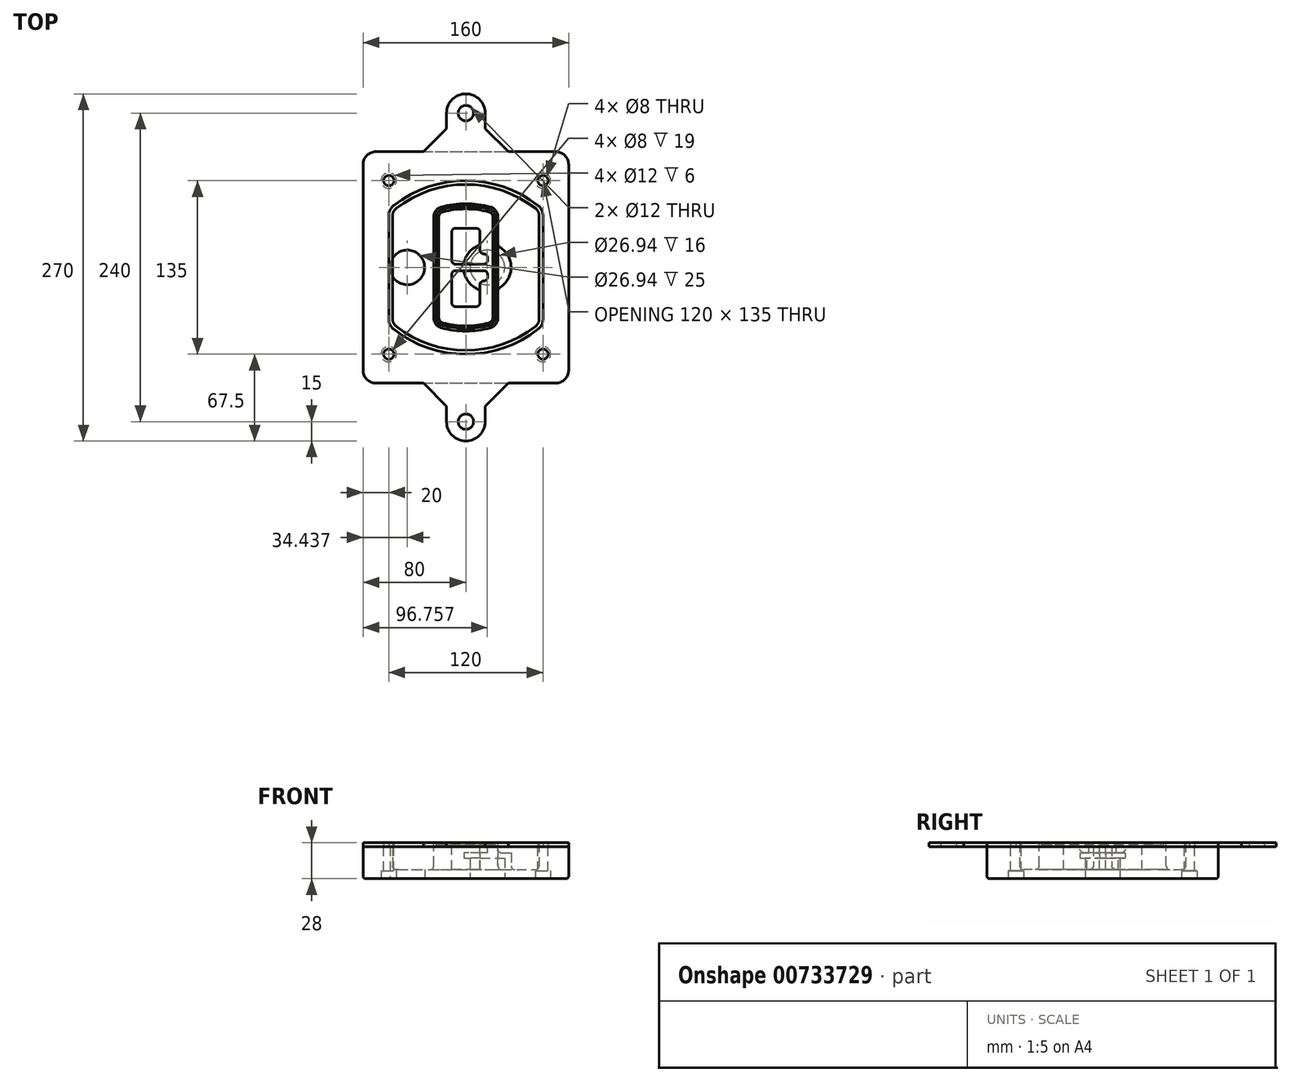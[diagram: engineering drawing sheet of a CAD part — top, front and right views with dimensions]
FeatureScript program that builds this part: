
annotation { "Feature Type Name" : "Feature", "Feature Type Description" : "" }
export const myFeature = defineFeature(function(context is Context, id is Id, definition is map)
    precondition{}
    {
        {
            var Q0;
            Q0=qCreatedBy(makeId("Top.planeOp"),FACE);
            var sketch = newSketch(context, id + "F0", { "sketchPlane" : qUnion([Q0])});
            skPoint(sketch, "E0.rect.middle", {"position": v(0, 0) * mm});
            skLineSegment(sketch, "E1.bottom", {"start": v(-70, -90) * mm, "end": v(70, -90) * mm});
            skLineSegment(sketch, "E1.top", {"start": v(-70, 90) * mm, "end": v(70, 90) * mm});
            skLineSegment(sketch, "E1.left", {"start": v(-80, -80) * mm, "end": v(-80, 80) * mm});
            skLineSegment(sketch, "E1.right", {"start": v(80, -80) * mm, "end": v(80, 80) * mm});
            skLineSegment(sketch, "E2", {"start": v(-80, 90) * mm, "end": v(80, -90) * mm, "construction": true});
            skLineSegment(sketch, "E3", {"start": v(80, 90) * mm, "end": v(-80, -90) * mm, "construction": true});
            skCircle(sketch, "E4", {"center": v(-60, 67.5) * mm, "radius": 4 * mm});
            skCircle(sketch, "E5", {"center": v(60, 67.5) * mm, "radius": 4 * mm});
            skCircle(sketch, "E6", {"center": v(60, -67.5) * mm, "radius": 4 * mm});
            skCircle(sketch, "E7", {"center": v(-60, -67.5) * mm, "radius": 4 * mm});
            skLineSegment(sketch, "E8", {"start": v(-60, 67.5) * mm, "end": v(60, 67.5) * mm, "construction": true});
            skLineSegment(sketch, "E9", {"start": v(60, 67.5) * mm, "end": v(60, -67.5) * mm, "construction": true});
            skLineSegment(sketch, "E10", {"start": v(60, -67.5) * mm, "end": v(-60, -67.5) * mm, "construction": true});
            skLineSegment(sketch, "E11", {"start": v(-60, -67.5) * mm, "end": v(-60, 67.5) * mm, "construction": true});
            skLineSegment(sketch, "E12", {"start": v(-60, 40.3) * mm, "end": v(-60, -40.3) * mm});
            skLineSegment(sketch, "E13", {"start": v(60, 40.3) * mm, "end": v(60, -40.3) * mm});
            skArc(sketch, "E14", {"start": v(56.15, 48.18) * mm, "mid": v(0, 67.5) * mm, "end": v(-56.15, 48.18) * mm});
            skArc(sketch, "E15", {"start": v(-56.15, -48.18) * mm, "mid": v(0, -67.5) * mm, "end": v(56.15, -48.18) * mm});
            skLineSegment(sketch, "E16", {"start": v(-60, 0) * mm, "end": v(60, 0) * mm, "construction": true});
            skPoint(sketch, "E17.visualSharp", {"position": v(-60, -45) * mm});
            skArc(sketch, "E17.filletArc", {"start": v(-60, -40.3) * mm, "mid": v(-58.99, -44.68) * mm, "end": v(-56.15, -48.18) * mm});
            skPoint(sketch, "E18.visualSharp", {"position": v(-60, 45) * mm});
            skArc(sketch, "E18.filletArc", {"start": v(-56.15, 48.18) * mm, "mid": v(-58.99, 44.68) * mm, "end": v(-60, 40.3) * mm});
            skPoint(sketch, "E19.visualSharp", {"position": v(60, 45) * mm});
            skArc(sketch, "E19.filletArc", {"start": v(60, 40.3) * mm, "mid": v(58.99, 44.68) * mm, "end": v(56.15, 48.18) * mm});
            skPoint(sketch, "E20.visualSharp", {"position": v(60, -45) * mm});
            skArc(sketch, "E20.filletArc", {"start": v(56.15, -48.18) * mm, "mid": v(58.99, -44.68) * mm, "end": v(60, -40.3) * mm});
            skPoint(sketch, "E21.visualSharp", {"position": v(-80, 90) * mm});
            skArc(sketch, "E21.filletArc", {"start": v(-70, 90) * mm, "mid": v(-77.07, 87.07) * mm, "end": v(-80, 80) * mm});
            skPoint(sketch, "E22.visualSharp", {"position": v(80, 90) * mm});
            skArc(sketch, "E22.filletArc", {"start": v(80, 80) * mm, "mid": v(77.07, 87.07) * mm, "end": v(70, 90) * mm});
            skPoint(sketch, "E23.visualSharp", {"position": v(80, -90) * mm});
            skArc(sketch, "E23.filletArc", {"start": v(70, -90) * mm, "mid": v(77.07, -87.07) * mm, "end": v(80, -80) * mm});
            skPoint(sketch, "E24.visualSharp", {"position": v(-80, -90) * mm});
            skArc(sketch, "E24.filletArc", {"start": v(-80, -80) * mm, "mid": v(-77.07, -87.07) * mm, "end": v(-70, -90) * mm});
            skArc(sketch, "E25.0", {"start": v(57, 40.3) * mm, "mid": v(56.3, 43.36) * mm, "end": v(54.3, 45.81) * mm});
            skLineSegment(sketch, "E25.1", {"start": v(57, 40.3) * mm, "end": v(57, -40.3) * mm});
            skArc(sketch, "E25.2", {"start": v(54.3, -45.81) * mm, "mid": v(56.3, -43.36) * mm, "end": v(57, -40.3) * mm});
            skArc(sketch, "E25.3", {"start": v(-54.3, -45.81) * mm, "mid": v(0, -64.5) * mm, "end": v(54.3, -45.81) * mm});
            skArc(sketch, "E25.4", {"start": v(-57, -40.3) * mm, "mid": v(-56.3, -43.36) * mm, "end": v(-54.3, -45.81) * mm});
            skArc(sketch, "E25.5", {"start": v(54.3, 45.81) * mm, "mid": v(0, 64.5) * mm, "end": v(-54.3, 45.81) * mm});
            skLineSegment(sketch, "E25.6", {"start": v(-57, 40.3) * mm, "end": v(-57, -40.3) * mm});
            skArc(sketch, "E25.7", {"start": v(-54.3, 45.81) * mm, "mid": v(-56.3, 43.36) * mm, "end": v(-57, 40.3) * mm});
            skArc(sketch, "E26.0", {"start": v(-58.62, 51.33) * mm, "mid": v(-62.58, 46.43) * mm, "end": v(-64, 40.3) * mm});
            skArc(sketch, "E26.1", {"start": v(58.62, 51.33) * mm, "mid": v(0, 71.5) * mm, "end": v(-58.62, 51.33) * mm});
            skArc(sketch, "E26.2", {"start": v(64, 40.3) * mm, "mid": v(62.58, 46.43) * mm, "end": v(58.62, 51.33) * mm});
            skLineSegment(sketch, "E26.3", {"start": v(64, 40.3) * mm, "end": v(64, -40.3) * mm});
            skArc(sketch, "E26.4", {"start": v(58.62, -51.33) * mm, "mid": v(62.58, -46.43) * mm, "end": v(64, -40.3) * mm});
            skLineSegment(sketch, "E26.5", {"start": v(-64, 40.3) * mm, "end": v(-64, -40.3) * mm});
            skArc(sketch, "E26.6", {"start": v(-58.62, -51.33) * mm, "mid": v(0, -71.5) * mm, "end": v(58.62, -51.33) * mm});
            skArc(sketch, "E26.7", {"start": v(-64, -40.3) * mm, "mid": v(-62.58, -46.43) * mm, "end": v(-58.62, -51.33) * mm});
            skSolve(sketch);
        }
        {
            var Q0;
            Q0=makeQuery(id+"F0.imprint","IMPRINT",FACE,{"disambiguationData":[TD([[makeQuery(id+"F0.imprint","IMPRINT",EDGE,{"derivedFrom":sQuery(id+"F0.wireOp",EDGE,"E1.bottom")}),1.0]])]});
            var Q1;
            Q1=makeQuery(id+"F0.imprint","IMPRINT",FACE,{"disambiguationData":[TD([[makeQuery(id+"F0.imprint","IMPRINT",EDGE,{"derivedFrom":sQuery(id+"F0.wireOp",EDGE,"E12")}),1.0]])]});
            var Q2;
            Q2=makeQuery(id+"F0.imprint","IMPRINT",FACE,{"disambiguationData":[TD([[makeQuery(id+"F0.imprint","IMPRINT",EDGE,{"derivedFrom":sQuery(id+"F0.wireOp",EDGE,"E25.0")}),1.0]])]});
            var Q3;
            Q3=makeQuery(id+"F0.imprint","IMPRINT",FACE,{"disambiguationData":[TD([[makeQuery(id+"F0.imprint","IMPRINT",EDGE,{"derivedFrom":sQuery(id+"F0.wireOp",EDGE,"E12")}),-1.0]])]});
            extrude(context, id + "F1", {"entities" : qUnion([Q0, Q1, Q2, Q3]), "oppositeDirection" : true, "depth" : 25 * mm});
        }
        {
            var Q0;
            Q0=makeQuery(id+"F0.imprint","IMPRINT",FACE,{"disambiguationData":[TD([[makeQuery(id+"F0.imprint","IMPRINT",EDGE,{"derivedFrom":sQuery(id+"F0.wireOp",EDGE,"E12")}),1.0]])]});
            extrude(context, id + "F2", {"entities" : qUnion([Q0]), "operationType" : NewBodyOperationType.ADD, "depth" : 3 * mm});
        }
        {
            var Q0;
            Q0=makeQuery(id+"F0.imprint","IMPRINT",FACE,{"disambiguationData":[TD([[makeQuery(id+"F0.imprint","IMPRINT",EDGE,{"derivedFrom":sQuery(id+"F0.wireOp",EDGE,"E25.0")}),1.0]])]});
            extrude(context, id + "F3", {"entities" : qUnion([Q0]), "operationType" : NewBodyOperationType.REMOVE, "oppositeDirection" : true, "depth" : 18 * mm});
        }
        {
            var Q0;
            Q0=makeQuery(id+"F2.opExtrude","CAP_FACE",FACE,{"disambiguationData":[OSD([sQuery(id+"F0.wireOp",EDGE,"E12"),sQuery(id+"F0.wireOp",EDGE,"E13"),sQuery(id+"F0.wireOp",EDGE,"E14"),sQuery(id+"F0.wireOp",EDGE,"E15"),sQuery(id+"F0.wireOp",EDGE,"E17.filletArc"),sQuery(id+"F0.wireOp",EDGE,"E18.filletArc"),sQuery(id+"F0.wireOp",EDGE,"E19.filletArc"),sQuery(id+"F0.wireOp",EDGE,"E20.filletArc"),sQuery(id+"F0.wireOp",EDGE,"E25.0"),sQuery(id+"F0.wireOp",EDGE,"E25.1"),sQuery(id+"F0.wireOp",EDGE,"E25.2"),sQuery(id+"F0.wireOp",EDGE,"E25.3"),sQuery(id+"F0.wireOp",EDGE,"E25.4"),sQuery(id+"F0.wireOp",EDGE,"E25.5"),sQuery(id+"F0.wireOp",EDGE,"E25.6"),sQuery(id+"F0.wireOp",EDGE,"E25.7")])],"isStart":false});
            var sketch = newSketch(context, id + "F4", { "sketchPlane" : qUnion([Q0])});
            skArc(sketch, "E27.0", {"start": v(-19.08, -46.97) * mm, "mid": v(0, -49.5) * mm, "end": v(19.08, -46.97) * mm});
            skArc(sketch, "E28.0", {"start": v(19.08, 46.97) * mm, "mid": v(0, 49.5) * mm, "end": v(-19.08, 46.97) * mm});
            skLineSegment(sketch, "E29", {"start": v(-25, 39.25) * mm, "end": v(-25, -39.25) * mm});
            skLineSegment(sketch, "E30", {"start": v(25, 39.25) * mm, "end": v(25, -39.25) * mm});
            skLineSegment(sketch, "E31", {"start": v(-25, 45.1) * mm, "end": v(25, 45.1) * mm, "construction": true});
            skLineSegment(sketch, "E32", {"start": v(-25, -45.1) * mm, "end": v(25, -45.1) * mm, "construction": true});
            skPoint(sketch, "E33.visualSharp", {"position": v(-25, 45.1) * mm});
            skArc(sketch, "E33.filletArc", {"start": v(-19.08, 46.97) * mm, "mid": v(-23.35, 44.11) * mm, "end": v(-25, 39.25) * mm});
            skPoint(sketch, "E34.visualSharp", {"position": v(25, 45.1) * mm});
            skArc(sketch, "E34.filletArc", {"start": v(25, 39.25) * mm, "mid": v(23.35, 44.11) * mm, "end": v(19.08, 46.97) * mm});
            skPoint(sketch, "E35.visualSharp", {"position": v(25, -45.1) * mm});
            skArc(sketch, "E35.filletArc", {"start": v(19.08, -46.97) * mm, "mid": v(23.35, -44.11) * mm, "end": v(25, -39.25) * mm});
            skPoint(sketch, "E36.visualSharp", {"position": v(-25, -45.1) * mm});
            skArc(sketch, "E36.filletArc", {"start": v(-25, -39.25) * mm, "mid": v(-23.35, -44.11) * mm, "end": v(-19.08, -46.97) * mm});
            skArc(sketch, "E37.0", {"start": v(54.3, 45.81) * mm, "mid": v(0, 64.5) * mm, "end": v(-54.3, 45.81) * mm});
            skArc(sketch, "E37.1", {"start": v(-54.3, 45.81) * mm, "mid": v(-56.3, 43.36) * mm, "end": v(-57, 40.3) * mm});
            skLineSegment(sketch, "E37.2", {"start": v(-57, 40.3) * mm, "end": v(-57, -40.3) * mm});
            skArc(sketch, "E37.3", {"start": v(-57, -40.3) * mm, "mid": v(-56.3, -43.36) * mm, "end": v(-54.3, -45.81) * mm});
            skArc(sketch, "E37.4", {"start": v(-54.3, -45.81) * mm, "mid": v(0, -64.5) * mm, "end": v(54.3, -45.81) * mm});
            skArc(sketch, "E37.5", {"start": v(54.3, -45.81) * mm, "mid": v(56.3, -43.36) * mm, "end": v(57, -40.3) * mm});
            skLineSegment(sketch, "E37.6", {"start": v(57, 40.3) * mm, "end": v(57, -40.3) * mm});
            skArc(sketch, "E37.7", {"start": v(57, 40.3) * mm, "mid": v(56.3, 43.36) * mm, "end": v(54.3, 45.81) * mm});
            skLineSegment(sketch, "E38.0", {"start": v(23, 39.25) * mm, "end": v(23, -39.25) * mm});
            skArc(sketch, "E38.1", {"start": v(18.56, -45.04) * mm, "mid": v(21.76, -42.9) * mm, "end": v(23, -39.25) * mm});
            skArc(sketch, "E38.2", {"start": v(-18.56, -45.04) * mm, "mid": v(0, -47.5) * mm, "end": v(18.56, -45.04) * mm});
            skArc(sketch, "E38.3", {"start": v(-23, -39.25) * mm, "mid": v(-21.76, -42.9) * mm, "end": v(-18.56, -45.04) * mm});
            skLineSegment(sketch, "E38.4", {"start": v(-23, 39.25) * mm, "end": v(-23, -39.25) * mm});
            skArc(sketch, "E38.5", {"start": v(23, 39.25) * mm, "mid": v(21.76, 42.9) * mm, "end": v(18.56, 45.04) * mm});
            skArc(sketch, "E38.6", {"start": v(-18.56, 45.04) * mm, "mid": v(-21.76, 42.9) * mm, "end": v(-23, 39.25) * mm});
            skArc(sketch, "E38.7", {"start": v(18.56, 45.04) * mm, "mid": v(0, 47.5) * mm, "end": v(-18.56, 45.04) * mm});
            skArc(sketch, "E39.0", {"start": v(21, 39.25) * mm, "mid": v(20.18, 41.68) * mm, "end": v(18.04, 43.1) * mm});
            skLineSegment(sketch, "E39.1", {"start": v(21, 39.25) * mm, "end": v(21, -39.25) * mm});
            skArc(sketch, "E39.2", {"start": v(18.04, -43.1) * mm, "mid": v(20.18, -41.68) * mm, "end": v(21, -39.25) * mm});
            skArc(sketch, "E39.3", {"start": v(-18.04, -43.1) * mm, "mid": v(0, -45.5) * mm, "end": v(18.04, -43.1) * mm});
            skArc(sketch, "E39.4", {"start": v(-21, -39.25) * mm, "mid": v(-20.18, -41.68) * mm, "end": v(-18.04, -43.1) * mm});
            skArc(sketch, "E39.5", {"start": v(18.04, 43.1) * mm, "mid": v(0, 45.5) * mm, "end": v(-18.04, 43.1) * mm});
            skLineSegment(sketch, "E39.6", {"start": v(-21, 39.25) * mm, "end": v(-21, -39.25) * mm});
            skArc(sketch, "E39.7", {"start": v(-18.04, 43.1) * mm, "mid": v(-20.18, 41.68) * mm, "end": v(-21, 39.25) * mm});
            skLineSegment(sketch, "E40", {"start": v(-25, 0) * mm, "end": v(25, 0) * mm, "construction": true});
            skLineSegment(sketch, "E41", {"start": v(-11, 5.5) * mm, "end": v(-11, 27.5) * mm});
            skLineSegment(sketch, "E42", {"start": v(-8, 30.5) * mm, "end": v(8, 30.5) * mm});
            skLineSegment(sketch, "E43", {"start": v(11, 27.5) * mm, "end": v(11, 13.5) * mm});
            skLineSegment(sketch, "E44", {"start": v(14, 10.5) * mm, "end": v(14, 10.5) * mm});
            skLineSegment(sketch, "E45", {"start": v(17, 7.5) * mm, "end": v(17, 5.5) * mm});
            skLineSegment(sketch, "E46", {"start": v(14, 2.5) * mm, "end": v(-8, 2.5) * mm});
            skPoint(sketch, "E47.visualSharp", {"position": v(-11, 30.5) * mm});
            skArc(sketch, "E47.filletArc", {"start": v(-8, 30.5) * mm, "mid": v(-10.12, 29.62) * mm, "end": v(-11, 27.5) * mm});
            skPoint(sketch, "E48.visualSharp", {"position": v(11, 30.5) * mm});
            skArc(sketch, "E48.filletArc", {"start": v(11, 27.5) * mm, "mid": v(10.12, 29.62) * mm, "end": v(8, 30.5) * mm});
            skPoint(sketch, "E49.visualSharp", {"position": v(11, 10.5) * mm});
            skArc(sketch, "E49.filletArc", {"start": v(11, 13.5) * mm, "mid": v(11.88, 11.38) * mm, "end": v(14, 10.5) * mm});
            skPoint(sketch, "E50.visualSharp", {"position": v(17, 10.5) * mm});
            skArc(sketch, "E50.filletArc", {"start": v(17, 7.5) * mm, "mid": v(16.12, 9.62) * mm, "end": v(14, 10.5) * mm});
            skPoint(sketch, "E51.visualSharp", {"position": v(17, 2.5) * mm});
            skArc(sketch, "E51.filletArc", {"start": v(14, 2.5) * mm, "mid": v(16.12, 3.38) * mm, "end": v(17, 5.5) * mm});
            skPoint(sketch, "E52.visualSharp", {"position": v(-11, 2.5) * mm});
            skArc(sketch, "E52.filletArc", {"start": v(-11, 5.5) * mm, "mid": v(-10.12, 3.38) * mm, "end": v(-8, 2.5) * mm});
            skLineSegment(sketch, "E53.0.MirrorCS", {"start": v(14, -2.5) * mm, "end": v(-8, -2.5) * mm});
            skArc(sketch, "E54.0.MirrorCS", {"start": v(-11, -5.5) * mm, "mid": v(-10.12, -3.38) * mm, "end": v(-8, -2.5) * mm});
            skLineSegment(sketch, "E55.0.MirrorCS", {"start": v(-11, -5.5) * mm, "end": v(-11, -27.5) * mm});
            skArc(sketch, "E56.0.MirrorCS", {"start": v(-8, -30.5) * mm, "mid": v(-10.12, -29.62) * mm, "end": v(-11, -27.5) * mm});
            skLineSegment(sketch, "E57.0.MirrorCS", {"start": v(-8, -30.5) * mm, "end": v(8, -30.5) * mm});
            skArc(sketch, "E58.0.MirrorCS", {"start": v(11, -27.5) * mm, "mid": v(10.12, -29.62) * mm, "end": v(8, -30.5) * mm});
            skLineSegment(sketch, "E59.0.MirrorCS", {"start": v(11, -27.5) * mm, "end": v(11, -13.5) * mm});
            skArc(sketch, "E60.0.MirrorCS", {"start": v(11, -13.5) * mm, "mid": v(11.88, -11.38) * mm, "end": v(14, -10.5) * mm});
            skArc(sketch, "E61.0.MirrorCS", {"start": v(17, -7.5) * mm, "mid": v(16.12, -9.62) * mm, "end": v(14, -10.5) * mm});
            skLineSegment(sketch, "E62.0.MirrorCS", {"start": v(17, -7.5) * mm, "end": v(17, -5.5) * mm});
            skArc(sketch, "E63.0.MirrorCS", {"start": v(14, -2.5) * mm, "mid": v(16.12, -3.38) * mm, "end": v(17, -5.5) * mm});
            skSolve(sketch);
        }
        {
            var Q0;
            Q0=makeQuery(id+"F4.imprint","IMPRINT",FACE,{"disambiguationData":[TD([[makeQuery(id+"F4.imprint","IMPRINT",EDGE,{"derivedFrom":sQuery(id+"F4.wireOp",EDGE,"E27.0")}),1.0]])]});
            var Q1;
            Q1=makeQuery(id+"F4.imprint","IMPRINT",FACE,{"disambiguationData":[TD([[makeQuery(id+"F4.imprint","IMPRINT",EDGE,{"derivedFrom":sQuery(id+"F4.wireOp",EDGE,"E38.0")}),-1.0]])]});
            var Q2;
            Q2=makeQuery(id+"F4.imprint","IMPRINT",FACE,{"disambiguationData":[TD([[makeQuery(id+"F4.imprint","IMPRINT",EDGE,{"derivedFrom":sQuery(id+"F4.wireOp",EDGE,"E39.0")}),1.0]])]});
            extrude(context, id + "F5", {"entities" : qUnion([Q0, Q1, Q2]), "operationType" : NewBodyOperationType.ADD, "endBound" : BoundingType.UP_TO_NEXT, "oppositeDirection" : true, "depth" : 25 * mm});
        }
        {
            var Q0;
            Q0=makeQuery(id+"F4.imprint","IMPRINT",FACE,{"disambiguationData":[TD([[makeQuery(id+"F4.imprint","IMPRINT",EDGE,{"derivedFrom":sQuery(id+"F4.wireOp",EDGE,"E38.0")}),-1.0]])]});
            extrude(context, id + "F6", {"entities" : qUnion([Q0]), "operationType" : NewBodyOperationType.REMOVE, "oppositeDirection" : true, "depth" : 2 * mm});
        }
        {
            var Q0;
            Q0=makeQuery(id+"F1.opExtrude","CAP_FACE",FACE,{"disambiguationData":[OSD([sQuery(id+"F0.wireOp",EDGE,"E1.bottom"),sQuery(id+"F0.wireOp",EDGE,"E1.top"),sQuery(id+"F0.wireOp",EDGE,"E1.left"),sQuery(id+"F0.wireOp",EDGE,"E1.right"),sQuery(id+"F0.wireOp",EDGE,"E4"),sQuery(id+"F0.wireOp",EDGE,"E5"),sQuery(id+"F0.wireOp",EDGE,"E6"),sQuery(id+"F0.wireOp",EDGE,"E7"),sQuery(id+"F0.wireOp",EDGE,"E21.filletArc"),sQuery(id+"F0.wireOp",EDGE,"E22.filletArc"),sQuery(id+"F0.wireOp",EDGE,"E23.filletArc"),sQuery(id+"F0.wireOp",EDGE,"E24.filletArc")])],"isStart":false});
            var sketch = newSketch(context, id + "F7", { "sketchPlane" : qUnion([Q0])});
            skCircle(sketch, "E64", {"center": v(16.76, 0) * mm, "radius": 13.47 * mm});
            skCircle(sketch, "E65", {"center": v(-45.56, 0) * mm, "radius": 13.47 * mm});
            skLineSegment(sketch, "E66", {"start": v(80, 0) * mm, "end": v(-80, 0) * mm});
            skCircle(sketch, "E67", {"center": v(16.76, 0) * mm, "radius": 18.47 * mm});
            skCircle(sketch, "E68", {"center": v(60, -67.5) * mm, "radius": 6 * mm});
            skCircle(sketch, "E69", {"center": v(-60, -67.5) * mm, "radius": 6 * mm});
            skCircle(sketch, "E70", {"center": v(-60, 67.5) * mm, "radius": 6 * mm});
            skCircle(sketch, "E71", {"center": v(60, 67.5) * mm, "radius": 6 * mm});
            skSolve(sketch);
        }
        {
            var Q0;
            {var subQ1=sQuery(id+"F7.wireOp",EDGE,"E66");var subQ4=sQuery(id+"F7.wireOp",EDGE,"E64");var subQ6=makeQuery(id+"F7.imprint","INTERSECT",VERTEX,{"disambiguationData":[OD(0.0)],"derivedFrom":[subQ4,subQ1]});Q0=makeQuery(id+"F7.imprint","IMPRINT",FACE,{"disambiguationData":[TD([[makeQuery(id+"F7.imprint","IMPRINT",EDGE,{"disambiguationData":[TD([[subQ6,-1.0]])],"derivedFrom":subQ4}),-1.0]])]});}
            var Q1;
            {var subQ0=sQuery(id+"F7.wireOp",EDGE,"E66");var subQ1=sQuery(id+"F7.wireOp",EDGE,"E64");var subQ3=makeQuery(id+"F7.imprint","INTERSECT",VERTEX,{"disambiguationData":[OD(0.0)],"derivedFrom":[subQ1,subQ0]});Q1=makeQuery(id+"F7.imprint","IMPRINT",FACE,{"disambiguationData":[TD([[makeQuery(id+"F7.imprint","IMPRINT",EDGE,{"disambiguationData":[TD([[subQ3,-1.0]])],"derivedFrom":subQ1}),1.0]])]});}
            var Q2;
            {var subQ0=sQuery(id+"F7.wireOp",EDGE,"E66");var subQ1=sQuery(id+"F7.wireOp",EDGE,"E64");var subQ3=makeQuery(id+"F7.imprint","INTERSECT",VERTEX,{"disambiguationData":[OD(0.0)],"derivedFrom":[subQ1,subQ0]});Q2=makeQuery(id+"F7.imprint","IMPRINT",FACE,{"disambiguationData":[TD([[makeQuery(id+"F7.imprint","IMPRINT",EDGE,{"disambiguationData":[TD([[subQ3,1.0]])],"derivedFrom":subQ1}),1.0]])]});}
            var Q3;
            {var subQ1=sQuery(id+"F7.wireOp",EDGE,"E66");var subQ4=sQuery(id+"F7.wireOp",EDGE,"E64");var subQ6=makeQuery(id+"F7.imprint","INTERSECT",VERTEX,{"disambiguationData":[OD(0.0)],"derivedFrom":[subQ4,subQ1]});Q3=makeQuery(id+"F7.imprint","IMPRINT",FACE,{"disambiguationData":[TD([[makeQuery(id+"F7.imprint","IMPRINT",EDGE,{"disambiguationData":[TD([[subQ6,1.0]])],"derivedFrom":subQ4}),-1.0]])]});}
            extrude(context, id + "F8", {"entities" : qUnion([Q0, Q1, Q2, Q3]), "operationType" : NewBodyOperationType.ADD, "oppositeDirection" : true, "depth" : 20 * mm});
        }
        {
            var Q0;
            {var subQ0=sQuery(id+"F7.wireOp",EDGE,"E66");var subQ1=sQuery(id+"F7.wireOp",EDGE,"E64");var subQ3=makeQuery(id+"F7.imprint","INTERSECT",VERTEX,{"disambiguationData":[OD(0.0)],"derivedFrom":[subQ1,subQ0]});Q0=makeQuery(id+"F7.imprint","IMPRINT",FACE,{"disambiguationData":[TD([[makeQuery(id+"F7.imprint","IMPRINT",EDGE,{"disambiguationData":[TD([[subQ3,-1.0]])],"derivedFrom":subQ1}),1.0]])]});}
            var Q1;
            {var subQ0=sQuery(id+"F7.wireOp",EDGE,"E66");var subQ1=sQuery(id+"F7.wireOp",EDGE,"E64");var subQ3=makeQuery(id+"F7.imprint","INTERSECT",VERTEX,{"disambiguationData":[OD(0.0)],"derivedFrom":[subQ1,subQ0]});Q1=makeQuery(id+"F7.imprint","IMPRINT",FACE,{"disambiguationData":[TD([[makeQuery(id+"F7.imprint","IMPRINT",EDGE,{"disambiguationData":[TD([[subQ3,1.0]])],"derivedFrom":subQ1}),1.0]])]});}
            extrude(context, id + "F9", {"entities" : qUnion([Q0, Q1]), "operationType" : NewBodyOperationType.REMOVE, "oppositeDirection" : true, "depth" : 16 * mm});
        }
        {
            var Q0;
            {var subQ0=sQuery(id+"F7.wireOp",EDGE,"E66");var subQ1=sQuery(id+"F7.wireOp",EDGE,"E65");var subQ3=makeQuery(id+"F7.imprint","INTERSECT",VERTEX,{"disambiguationData":[OD(0.0)],"derivedFrom":[subQ1,subQ0]});Q0=makeQuery(id+"F7.imprint","IMPRINT",FACE,{"disambiguationData":[TD([[makeQuery(id+"F7.imprint","IMPRINT",EDGE,{"disambiguationData":[TD([[subQ3,-1.0]])],"derivedFrom":subQ1}),1.0]])]});}
            var Q1;
            {var subQ0=sQuery(id+"F7.wireOp",EDGE,"E66");var subQ1=sQuery(id+"F7.wireOp",EDGE,"E65");var subQ3=makeQuery(id+"F7.imprint","INTERSECT",VERTEX,{"disambiguationData":[OD(0.0)],"derivedFrom":[subQ1,subQ0]});Q1=makeQuery(id+"F7.imprint","IMPRINT",FACE,{"disambiguationData":[TD([[makeQuery(id+"F7.imprint","IMPRINT",EDGE,{"disambiguationData":[TD([[subQ3,1.0]])],"derivedFrom":subQ1}),1.0]])]});}
            extrude(context, id + "F10", {"entities" : qUnion([Q0, Q1]), "operationType" : NewBodyOperationType.REMOVE, "oppositeDirection" : true, "depth" : 25 * mm});
        }
        {
            var Q0;
            Q0=makeQuery(id+"F7.imprint","IMPRINT",FACE,{"disambiguationData":[TD([[makeQuery(id+"F7.imprint","IMPRINT",EDGE,{"derivedFrom":sQuery(id+"F7.wireOp",EDGE,"E68")}),1.0]])]});
            var Q1;
            Q1=makeQuery(id+"F7.imprint","IMPRINT",FACE,{"disambiguationData":[TD([[makeQuery(id+"F7.imprint","IMPRINT",EDGE,{"derivedFrom":makeQuery(id+"F1.opExtrude","CAP_EDGE",EDGE,{"disambiguationData":[OSD([sQuery(id+"F0.wireOp",EDGE,"E5")])],"isStart":false})}),-1.0]])]});
            var Q2;
            Q2=makeQuery(id+"F7.imprint","IMPRINT",FACE,{"disambiguationData":[TD([[makeQuery(id+"F7.imprint","IMPRINT",EDGE,{"derivedFrom":sQuery(id+"F7.wireOp",EDGE,"E69")}),1.0]])]});
            var Q3;
            Q3=makeQuery(id+"F7.imprint","IMPRINT",FACE,{"disambiguationData":[TD([[makeQuery(id+"F7.imprint","IMPRINT",EDGE,{"derivedFrom":makeQuery(id+"F1.opExtrude","CAP_EDGE",EDGE,{"disambiguationData":[OSD([sQuery(id+"F0.wireOp",EDGE,"E4")])],"isStart":false})}),-1.0]])]});
            var Q4;
            Q4=makeQuery(id+"F7.imprint","IMPRINT",FACE,{"disambiguationData":[TD([[makeQuery(id+"F7.imprint","IMPRINT",EDGE,{"derivedFrom":sQuery(id+"F7.wireOp",EDGE,"E70")}),1.0]])]});
            var Q5;
            Q5=makeQuery(id+"F7.imprint","IMPRINT",FACE,{"disambiguationData":[TD([[makeQuery(id+"F7.imprint","IMPRINT",EDGE,{"derivedFrom":makeQuery(id+"F1.opExtrude","CAP_EDGE",EDGE,{"disambiguationData":[OSD([sQuery(id+"F0.wireOp",EDGE,"E7")])],"isStart":false})}),-1.0]])]});
            var Q6;
            Q6=makeQuery(id+"F7.imprint","IMPRINT",FACE,{"disambiguationData":[TD([[makeQuery(id+"F7.imprint","IMPRINT",EDGE,{"derivedFrom":sQuery(id+"F7.wireOp",EDGE,"E71")}),1.0]])]});
            var Q7;
            Q7=makeQuery(id+"F7.imprint","IMPRINT",FACE,{"disambiguationData":[TD([[makeQuery(id+"F7.imprint","IMPRINT",EDGE,{"derivedFrom":makeQuery(id+"F1.opExtrude","CAP_EDGE",EDGE,{"disambiguationData":[OSD([sQuery(id+"F0.wireOp",EDGE,"E6")])],"isStart":false})}),-1.0]])]});
            extrude(context, id + "F11", {"entities" : qUnion([Q0, Q1, Q2, Q3, Q4, Q5, Q6, Q7]), "operationType" : NewBodyOperationType.REMOVE, "oppositeDirection" : true, "depth" : 6 * mm});
        }
        {
            var Q0;
            Q0=makeQuery(id+"F9.boolean.opBoolean","COPY",FACE,{"derivedFrom":makeQuery(id+"F9.opExtrude","CAP_FACE",FACE,{"disambiguationData":[OSD([sQuery(id+"F7.wireOp",EDGE,"E64")])],"isStart":false})});
            var sketch = newSketch(context, id + "F12", { "sketchPlane" : qUnion([Q0])});
            skArc(sketch, "E72.0", {"start": v(11, 17.55) * mm, "mid": v(2.57, 11.82) * mm, "end": v(-1.54, 2.5) * mm});
            skArc(sketch, "E72.1", {"start": v(-1.54, -2.5) * mm, "mid": v(2.57, -11.82) * mm, "end": v(11, -17.55) * mm});
            skLineSegment(sketch, "E73", {"start": v(-1.54, -2.5) * mm, "end": v(14, -2.5) * mm});
            skLineSegment(sketch, "E74.0", {"start": v(14, 2.5) * mm, "end": v(-1.54, 2.5) * mm});
            skArc(sketch, "E74.1", {"start": v(14, 2.5) * mm, "mid": v(16.12, 3.38) * mm, "end": v(17, 5.5) * mm});
            skLineSegment(sketch, "E74.2", {"start": v(17, 7.5) * mm, "end": v(17, 5.5) * mm});
            skArc(sketch, "E74.3", {"start": v(17, 7.5) * mm, "mid": v(16.12, 9.62) * mm, "end": v(14, 10.5) * mm});
            skArc(sketch, "E74.4", {"start": v(11, 13.5) * mm, "mid": v(11.88, 11.38) * mm, "end": v(14, 10.5) * mm});
            skLineSegment(sketch, "E74.5", {"start": v(11, 17.55) * mm, "end": v(11, 13.5) * mm});
            skLineSegment(sketch, "E74.7", {"start": v(14, -2.5) * mm, "end": v(-1.54, -2.5) * mm});
            skArc(sketch, "E74.8", {"start": v(14, -2.5) * mm, "mid": v(16.12, -3.38) * mm, "end": v(17, -5.5) * mm});
            skLineSegment(sketch, "E74.9", {"start": v(17, -7.5) * mm, "end": v(17, -5.5) * mm});
            skArc(sketch, "E74.10", {"start": v(17, -7.5) * mm, "mid": v(16.12, -9.62) * mm, "end": v(14, -10.5) * mm});
            skArc(sketch, "E74.11", {"start": v(11, -13.5) * mm, "mid": v(11.88, -11.38) * mm, "end": v(14, -10.5) * mm});
            skLineSegment(sketch, "E74.12", {"start": v(11, -17.55) * mm, "end": v(11, -13.5) * mm});
            skPoint(sketch, "E75.orphan", {"position": v(11, -27.5) * mm});
            skPoint(sketch, "E76.orphan", {"position": v(-8, -2.5) * mm});
            skPoint(sketch, "E77.orphan", {"position": v(-8, 2.5) * mm});
            skPoint(sketch, "E78.orphan", {"position": v(11, 27.5) * mm});
            skSolve(sketch);
        }
        {
            var Q0;
            {var subQ7=sQuery(id+"F12.wireOp",EDGE,"E72.0");var subQ14=sQuery(id+"F12.wireOp",EDGE,"E72.1");var subQ16=sQuery(id+"F12.wireOp",EDGE,"E74.1");var subQ18=sQuery(id+"F12.wireOp",EDGE,"E74.8");Q0=qUnion([makeQuery(id+"F12.imprint","IMPRINT",FACE,{"disambiguationData":[TD([[makeQuery(id+"F12.imprint","IMPRINT",EDGE,{"derivedFrom":subQ7}),1.0]])]}),makeQuery(id+"F12.imprint","IMPRINT",FACE,{"disambiguationData":[TD([[makeQuery(id+"F12.imprint","IMPRINT",EDGE,{"derivedFrom":subQ14}),1.0]])]}),makeQuery(id+"F12.imprint","IMPRINT",FACE,{"disambiguationData":[TD([[makeQuery(id+"F12.imprint","IMPRINT",EDGE,{"derivedFrom":subQ16}),1.0]])]}),makeQuery(id+"F12.imprint","IMPRINT",FACE,{"disambiguationData":[TD([[makeQuery(id+"F12.imprint","IMPRINT",EDGE,{"derivedFrom":subQ18}),-1.0]])]})]);}
            var Q1;
            Q1=makeQuery(id+"F5.boolean.opBoolean","SPLIT",FACE,{"disambiguationData":[TD([makeQuery(id+"F5.opExtrude","SWEPT_FACE",FACE,{"disambiguationData":[OSD([sQuery(id+"F4.wireOp",EDGE,"E41")])]})])],"derivedFrom":makeQuery(id+"F3.boolean.opBoolean","COPY",FACE,{"derivedFrom":makeQuery(id+"F3.opExtrude","CAP_FACE",FACE,{"disambiguationData":[OSD([sQuery(id+"F0.wireOp",EDGE,"E25.0"),sQuery(id+"F0.wireOp",EDGE,"E25.1"),sQuery(id+"F0.wireOp",EDGE,"E25.2"),sQuery(id+"F0.wireOp",EDGE,"E25.3"),sQuery(id+"F0.wireOp",EDGE,"E25.4"),sQuery(id+"F0.wireOp",EDGE,"E25.5"),sQuery(id+"F0.wireOp",EDGE,"E25.6"),sQuery(id+"F0.wireOp",EDGE,"E25.7")])],"isStart":false})})});
            extrude(context, id + "F13", {"entities" : qUnion([Q0]), "operationType" : NewBodyOperationType.REMOVE, "endBound" : BoundingType.UP_TO_SURFACE, "endBoundEntityFace" : qUnion([Q1]), "depth" : 25 * mm});
        }
        {
            var Q0;
            Q0=makeQuery(id+"F3.boolean.opBoolean","COPY",EDGE,{"derivedFrom":makeQuery(id+"F3.opExtrude","CAP_EDGE",EDGE,{"disambiguationData":[OSD([sQuery(id+"F0.wireOp",EDGE,"E25.6")])],"isStart":false})});
            var Q1;
            Q1=makeQuery(id+"F8.boolean.opBoolean","INTERSECT",EDGE,{"derivedFrom":[makeQuery(id+"F5.opExtrude","SWEPT_FACE",FACE,{"disambiguationData":[OSD([sQuery(id+"F4.wireOp",EDGE,"E30")])]}),makeQuery(id+"F8.opExtrude","CAP_FACE",FACE,{"disambiguationData":[OSD([sQuery(id+"F7.wireOp",EDGE,"E67")])],"isStart":false})]});
            var Q2;
            Q2=makeQuery(id+"F8.boolean.opBoolean","INTERSECT",EDGE,{"disambiguationData":[OD(1.0)],"derivedFrom":[makeQuery(id+"F5.opExtrude","SWEPT_FACE",FACE,{"disambiguationData":[OSD([sQuery(id+"F4.wireOp",EDGE,"E30")])]}),makeQuery(id+"F8.opExtrude","SWEPT_FACE",FACE,{"disambiguationData":[OSD([sQuery(id+"F7.wireOp",EDGE,"E67")])]})]});
            var Q3;
            {var subQ0=sQuery(id+"F4.wireOp",EDGE,"E30");Q3=makeQuery(id+"F8.boolean.opBoolean","SPLIT",EDGE,{"disambiguationData":[TD([makeQuery(id+"F5.opExtrude","SWEPT_FACE",FACE,{"disambiguationData":[OSD([sQuery(id+"F4.wireOp",EDGE,"E35.filletArc")])]})])],"derivedFrom":makeQuery(id+"F5.opExtrude","CAP_EDGE",EDGE,{"disambiguationData":[OSD([subQ0])],"isStart":false})});}
            var Q4;
            {var subQ0=sQuery(id+"F0.wireOp",EDGE,"E25.7");var subQ1=sQuery(id+"F0.wireOp",EDGE,"E25.1");var subQ2=sQuery(id+"F0.wireOp",EDGE,"E25.6");var subQ3=sQuery(id+"F0.wireOp",EDGE,"E25.5");var subQ4=sQuery(id+"F0.wireOp",EDGE,"E25.4");var subQ5=sQuery(id+"F0.wireOp",EDGE,"E25.0");var subQ6=sQuery(id+"F0.wireOp",EDGE,"E25.2");var subQ7=sQuery(id+"F0.wireOp",EDGE,"E25.3");Q4=makeQuery(id+"F8.boolean.opBoolean","INTERSECT",EDGE,{"derivedFrom":[makeQuery(id+"F5.boolean.opBoolean","SPLIT",FACE,{"disambiguationData":[TD([makeQuery(id+"F2.opExtrude","SWEPT_FACE",FACE,{"disambiguationData":[OSD([subQ5])]})])],"derivedFrom":makeQuery(id+"F3.boolean.opBoolean","COPY",FACE,{"derivedFrom":makeQuery(id+"F3.opExtrude","CAP_FACE",FACE,{"disambiguationData":[OSD([subQ5,subQ1,subQ6,subQ7,subQ4,subQ3,subQ2,subQ0])],"isStart":false})})}),makeQuery(id+"F8.opExtrude","SWEPT_FACE",FACE,{"disambiguationData":[OSD([sQuery(id+"F7.wireOp",EDGE,"E67")])]})]});}
            var Q5;
            Q5=makeQuery(id+"F8.boolean.opBoolean","INTERSECT",EDGE,{"disambiguationData":[OD(0.0)],"derivedFrom":[makeQuery(id+"F5.opExtrude","SWEPT_FACE",FACE,{"disambiguationData":[OSD([sQuery(id+"F4.wireOp",EDGE,"E30")])]}),makeQuery(id+"F8.opExtrude","SWEPT_FACE",FACE,{"disambiguationData":[OSD([sQuery(id+"F7.wireOp",EDGE,"E67")])]})]});
            fillet(context, id + "F14", {"entities" : qUnion([Q0, Q1, Q2, Q3, Q4, Q5]), "radius" : 3 * mm, "tangentPropagation" : true, "allowEdgeOverflow" : false});
        }
        {
            var Q0;
            Q0=makeQuery(id+"F1.opExtrude","CAP_EDGE",EDGE,{"disambiguationData":[OSD([sQuery(id+"F0.wireOp",EDGE,"E1.bottom")])],"isStart":false});
            fillet(context, id + "F15", {"entities" : qUnion([Q0]), "radius" : 2 * mm, "tangentPropagation" : true, "allowEdgeOverflow" : false});
        }
        {
            var Q0;
            {var subQ0=sQuery(id+"F0.wireOp",EDGE,"E21.filletArc");var subQ1=sQuery(id+"F0.wireOp",EDGE,"E7");var subQ2=sQuery(id+"F0.wireOp",EDGE,"E6");var subQ3=sQuery(id+"F0.wireOp",EDGE,"E5");var subQ4=sQuery(id+"F0.wireOp",EDGE,"E4");var subQ5=sQuery(id+"F0.wireOp",EDGE,"E22.filletArc");var subQ6=sQuery(id+"F0.wireOp",EDGE,"E1.bottom");var subQ7=sQuery(id+"F0.wireOp",EDGE,"E1.right");var subQ8=sQuery(id+"F0.wireOp",EDGE,"E1.top");var subQ9=sQuery(id+"F0.wireOp",EDGE,"E1.left");var subQ10=sQuery(id+"F0.wireOp",EDGE,"E23.filletArc");var subQ11=sQuery(id+"F0.wireOp",EDGE,"E24.filletArc");Q0=makeQuery(id+"F2.boolean.opBoolean","SPLIT",FACE,{"disambiguationData":[TD([makeQuery(id+"F1.opExtrude","SWEPT_FACE",FACE,{"disambiguationData":[OSD([subQ6])]})])],"derivedFrom":makeQuery(id+"F1.opExtrude","CAP_FACE",FACE,{"disambiguationData":[OSD([subQ6,subQ8,subQ9,subQ7,subQ4,subQ3,subQ2,subQ1,subQ0,subQ5,subQ10,subQ11])],"isStart":true})});}
            var sketch = newSketch(context, id + "F16", { "sketchPlane" : qUnion([Q0])});
            skCircle(sketch, "E79", {"center": v(0, 120) * mm, "radius": 6 * mm});
            skArc(sketch, "E80", {"start": v(15, 120) * mm, "mid": v(0, 135) * mm, "end": v(-15, 120) * mm});
            skLineSegment(sketch, "E81", {"start": v(-15, 120) * mm, "end": v(-15, 108) * mm});
            skLineSegment(sketch, "E82", {"start": v(-15, 108) * mm, "end": v(-33, 90) * mm});
            skLineSegment(sketch, "E83", {"start": v(15, 120) * mm, "end": v(15, 108) * mm});
            skLineSegment(sketch, "E84", {"start": v(15, 108) * mm, "end": v(33, 90) * mm});
            skLineSegment(sketch, "E85", {"start": v(80, 0) * mm, "end": v(-80, 0) * mm, "construction": true});
            skLineSegment(sketch, "E86.MirrorCS", {"start": v(15, -108) * mm, "end": v(33, -90) * mm});
            skLineSegment(sketch, "E87.MirrorCS", {"start": v(15, -120) * mm, "end": v(15, -108) * mm});
            skArc(sketch, "E88.MirrorCS", {"start": v(15, -120) * mm, "mid": v(0, -135) * mm, "end": v(-15, -120) * mm});
            skLineSegment(sketch, "E89.MirrorCS", {"start": v(-15, -120) * mm, "end": v(-15, -108) * mm});
            skCircle(sketch, "E90.MirrorC", {"center": v(0, -120) * mm, "radius": 6 * mm});
            skLineSegment(sketch, "E91.MirrorCS", {"start": v(-15, -108) * mm, "end": v(-33, -90) * mm});
            skSolve(sketch);
        }
        {
            var Q0;
            Q0=makeQuery(id+"F16.imprint","IMPRINT",FACE,{"disambiguationData":[TD([[makeQuery(id+"F16.imprint","IMPRINT",EDGE,{"derivedFrom":sQuery(id+"F16.wireOp",EDGE,"E79")}),-1.0]])]});
            var Q1;
            Q1=makeQuery(id+"F16.imprint","IMPRINT",FACE,{"disambiguationData":[TD([[makeQuery(id+"F16.imprint","IMPRINT",EDGE,{"derivedFrom":makeQuery(id+"F1.opExtrude","CAP_EDGE",EDGE,{"disambiguationData":[OSD([sQuery(id+"F0.wireOp",EDGE,"E1.left")])],"isStart":true})}),-1.0]])]});
            var Q2;
            {var subQ0=sQuery(id+"F16.wireOp",EDGE,"E86.MirrorCS");Q2=makeQuery(id+"F16.imprint","IMPRINT",FACE,{"disambiguationData":[TD([[makeQuery(id+"F16.imprint","IMPRINT",EDGE,{"derivedFrom":subQ0}),1.0]])]});}
            var Q3;
            Q3=makeQuery(id+"F2.opExtrude","CAP_FACE",FACE,{"disambiguationData":[OSD([sQuery(id+"F0.wireOp",EDGE,"E12"),sQuery(id+"F0.wireOp",EDGE,"E13"),sQuery(id+"F0.wireOp",EDGE,"E14"),sQuery(id+"F0.wireOp",EDGE,"E15"),sQuery(id+"F0.wireOp",EDGE,"E17.filletArc"),sQuery(id+"F0.wireOp",EDGE,"E18.filletArc"),sQuery(id+"F0.wireOp",EDGE,"E19.filletArc"),sQuery(id+"F0.wireOp",EDGE,"E20.filletArc"),sQuery(id+"F0.wireOp",EDGE,"E25.0"),sQuery(id+"F0.wireOp",EDGE,"E25.1"),sQuery(id+"F0.wireOp",EDGE,"E25.2"),sQuery(id+"F0.wireOp",EDGE,"E25.3"),sQuery(id+"F0.wireOp",EDGE,"E25.4"),sQuery(id+"F0.wireOp",EDGE,"E25.5"),sQuery(id+"F0.wireOp",EDGE,"E25.6"),sQuery(id+"F0.wireOp",EDGE,"E25.7")])],"isStart":false});
            extrude(context, id + "F17", {"entities" : qUnion([Q0, Q1, Q2]), "endBound" : BoundingType.UP_TO_SURFACE, "depth" : 25 * mm, "endBoundEntityFace" : qUnion([Q3]), "offsetDistance" : 25 * mm});
        }
    });
